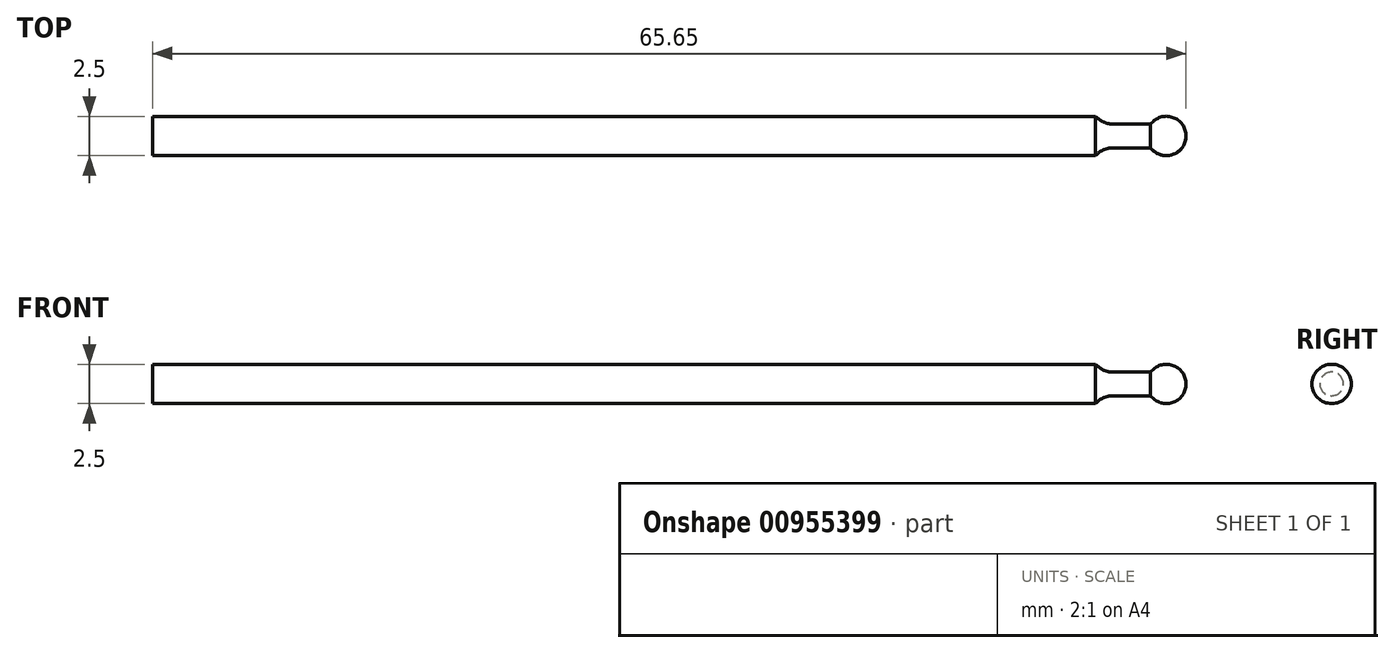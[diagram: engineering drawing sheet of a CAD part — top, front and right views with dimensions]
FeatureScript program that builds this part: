
annotation { "Feature Type Name" : "Feature", "Feature Type Description" : "" }
export const myFeature = defineFeature(function(context is Context, id is Id, definition is map)
    precondition{}
    {
        {
            var Q0;
            Q0=qCreatedBy(makeId("Top.planeOp"),FACE);
            var sketch = newSketch(context, id + "F0", { "sketchPlane" : qUnion([Q0])});
            skLineSegment(sketch, "E0", {"start": v(-60, 1.25) * mm, "end": v(-0.1, 1.25) * mm});
            skLineSegment(sketch, "E1", {"start": v(1.02, 0.75) * mm, "end": v(3.4, 0.75) * mm});
            skArc(sketch, "E2", {"start": v(-0.1, 1.25) * mm, "mid": v(0.4, 0.88) * mm, "end": v(1.02, 0.75) * mm});
            skArc(sketch, "E3", {"start": v(3.4, -0.75) * mm, "mid": v(5.65, 0) * mm, "end": v(3.4, 0.75) * mm});
            skLineSegment(sketch, "E4.MirrorCS", {"start": v(-60, -1.25) * mm, "end": v(-0.1, -1.25) * mm});
            skArc(sketch, "E5.MirrorCS", {"start": v(-0.1, -1.25) * mm, "mid": v(0.4, -0.88) * mm, "end": v(1.02, -0.75) * mm});
            skLineSegment(sketch, "E6.MirrorCS", {"start": v(1.02, -0.75) * mm, "end": v(3.4, -0.75) * mm});
            skLineSegment(sketch, "E7", {"start": v(-69.69, 0) * mm, "end": v(33.4, 0) * mm});
            skLineSegment(sketch, "E8", {"start": v(-60, 1.25) * mm, "end": v(-60, -1.25) * mm});
            skSolve(sketch);
        }
        {
            var Q0;
            {var subQ4=sQuery(id+"F0.wireOp",EDGE,"E0");Q0=makeQuery(id+"F0.imprint","IMPRINT",FACE,{"disambiguationData":[TD([[makeQuery(id+"F0.imprint","IMPRINT",EDGE,{"derivedFrom":subQ4}),-1.0]])]});}
            var Q1;
            Q1=sQuery(id+"F0.wireOp",EDGE,"E7");
            revolve(context, id + "F1", {"surfaceOperationType" : NewSurfaceOperationType.NEW, "entities" : qUnion([Q0]), "axis" : qUnion([Q1]), "revolveType" : RevolveType.FULL});
        }
    });
